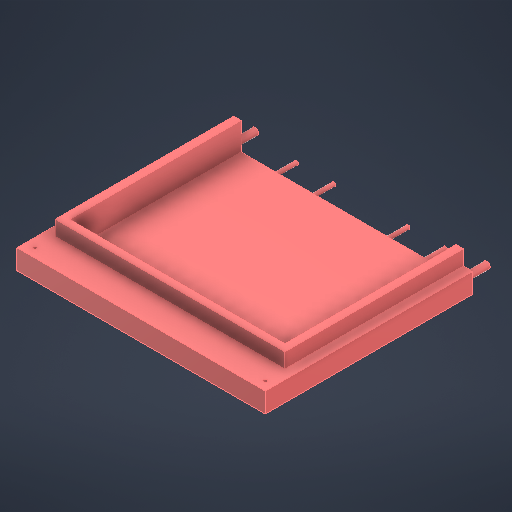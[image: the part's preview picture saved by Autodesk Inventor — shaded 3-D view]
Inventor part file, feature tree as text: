
AUTODESK INVENTOR PART (.ipt)
format: ipt  version: 2025.2 (Build 292293000, 293)  size: 321,536 bytes
history: native  units: in
note: dims shown in document units (in); Inventor stores cm internally (conversion verified against a paired STEP export)
features: sketch x10, extrude x7, split x3, plane x1
ambient origin geometry x8: Origin, YZ Plane, XZ Plane, XY Plane, X Axis, Y Axis, Z Axis, Center Point
bodies: Solid1 (feature_tree)
feature tree (21):
  extrude  "Extrusion1"  Depth=6.5748in
  extrude  "Extrusion2"  Depth=5.689in
  extrude  "Extrusion4"  Depth=0.3307in TaperAngle=0.0deg
  extrude  "Extrusion5"  Depth=0.2362in
  extrude  "Extrusion6"  Depth=0.0984in
  sketch  "Sketch8"  dims[d20=0.2362in d21=0.2362in]
  sketch  "Sketch9"  dims[d22=0.0984in d23=0.2362in]
  split  "Split1"
  split  "Split2"
  split  "Split3"
  plane  "Work Plane1"
  extrude  "Extrusion7"  Depth=0.2362in
  extrude  "Extrusion8"  Depth=0.2362in
  sketch  "Sketch1"  dims[d0=6.5748in d1=10.9843in]
  sketch  "Sketch2"  dims[d2=0.5276in d3=0.0in d4=5.689in]
  sketch  "Sketch4"  dims[d5=9.0591in d6=0.3307in d7=0.0in]
  sketch  "Sketch5"  dims[d16=0.0984in d17=0.2362in]
  sketch  "Sketch7"  dims[d18=0.2362in d19=0.0984in]
  sketch  "Sketch10"  dims[d24=0.2362in]
  sketch  "Sketch11"  dims[d25=0.0984in]
  sketch  "Sketch12"  dims[d26=0.2362in d27=0.2362in d28=0.3937in d29=0.0in d30=0.1969in d31=0.1969in d32=9.4528in d33=0.1969in d34=0.1969in d35=9.4528in d36=0.3937in d37=0.0in d42=0.1378in d43=0.1378in d44=0.1378in d45=0.1378in d46=0.4488in d47=0.0in d48=6.5812in d49=0.0in d51=0.187in d53=0.187in d55=0.1083in d57=0.1083in d59=0.1083in d61=0.1083in d62=0.5906in d63=0.0in d50=0.0197in]
